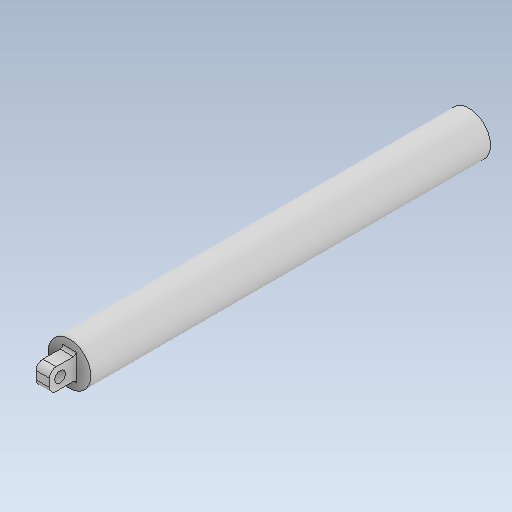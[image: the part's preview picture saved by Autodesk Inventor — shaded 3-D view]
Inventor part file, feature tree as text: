
AUTODESK INVENTOR PART (.ipt)
format: ipt  version: 2021 (Build 250183000, 183)  size: 121,856 bytes
history: native  units: mm
features: extrude x2, fillet x2, sketch x2, hole x1
ambient origin geometry x8: Origin, YZ Plane, XZ Plane, XY Plane, X Axis, Y Axis, Z Axis, Center Point
bodies: Body1 (feature_tree)
feature tree (7):
  extrude  "Extrusion3"  Depth=300.0mm TaperAngle=0.0deg
  extrude  "Extrusion4"  Depth=2.0mm
  fillet  "Fillet1"  Radius=20.0mm
  fillet  "Fillet2"  Radius=10.0mm
  hole  "Hole1"  [1 undecoded]
  sketch  "Sketch3"  dims[d6=32.0mm d7=300.0mm d8=0.0mm]
  sketch  "Sketch4"  dims[d9=8.0mm d10=8.0mm d11=20.0mm d12=10.0mm d13=0.0mm d14=2.0mm d15=5.0mm d16=8.0mm d17=8.0mm d18=6.0mm d19=4.0mm d20=2.0mm d21=90.0deg d22=8.0mm d23=20.594885mm d4=0.5mm d5=0.872665mm]
note: 1 required parameter value undecoded (feature->parameter linkage not recoverable at this tier; creation-order binding heuristic only, values carry confidence <= 0.55)
